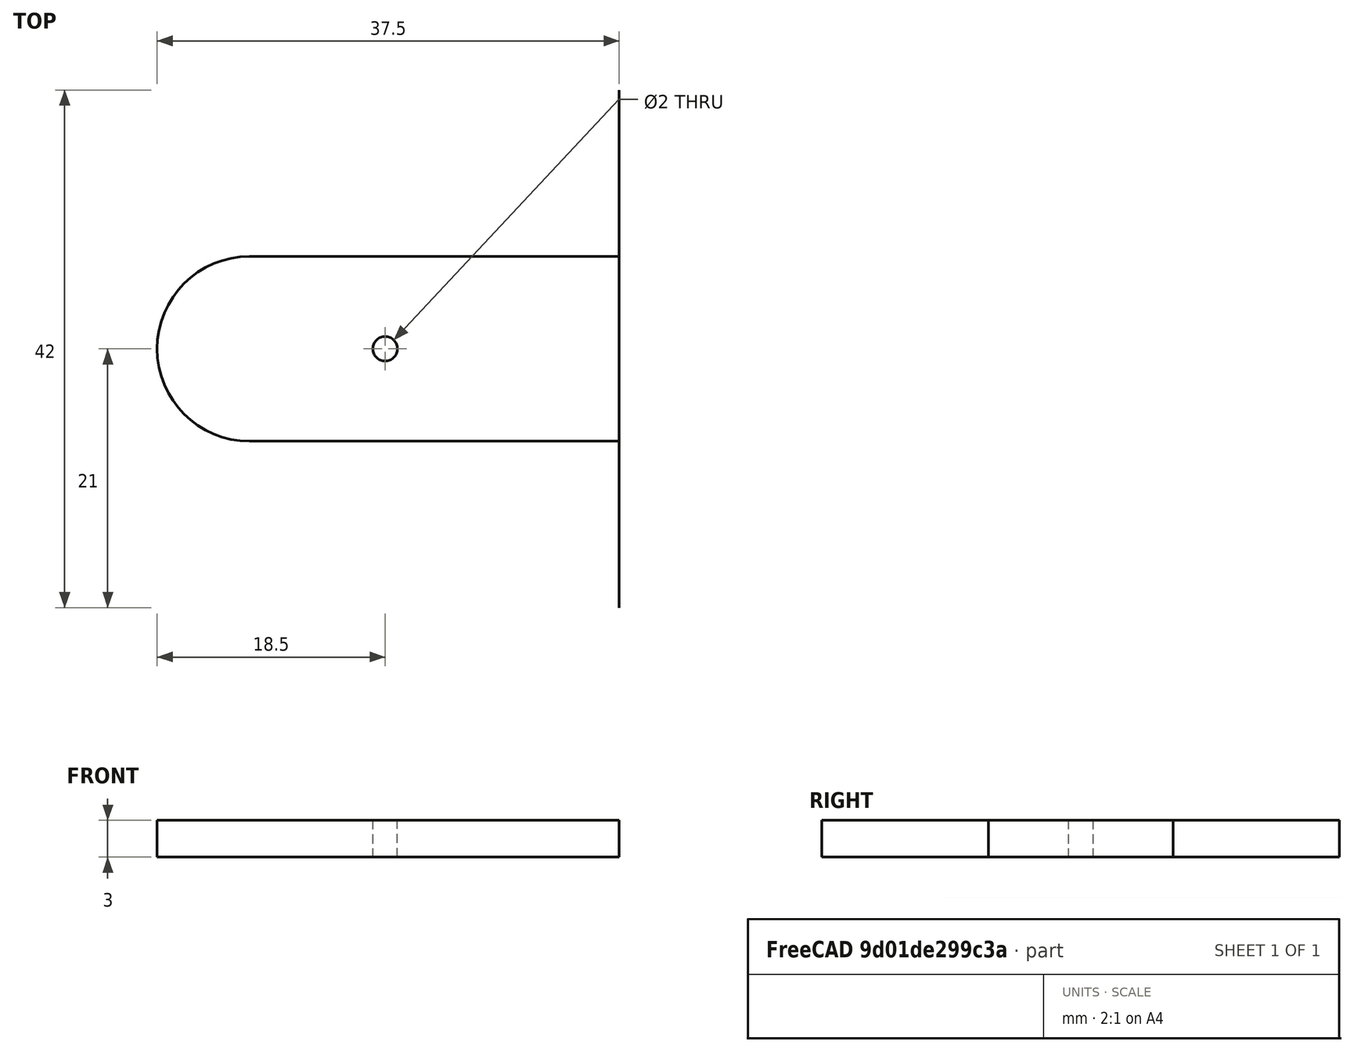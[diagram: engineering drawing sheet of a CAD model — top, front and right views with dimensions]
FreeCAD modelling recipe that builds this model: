
FCSTD DOCUMENT  (FreeCAD 0.18R4 (GitTag))
Label: Horizontal Servo Base
License: All rights reserved
LicenseURL: http://en.wikipedia.org/wiki/All_rights_reserved
objects: Sketcher::SketchObject×1, Part::Extrusion×1
note: 2 computed .brp shape members not serialized (recipe doc carries the construction recipe); baked Part::Feature solids carry a one-line shape summary decoded from their .brp

FEATURE [Sketcher::SketchObject] Sketch
  sketch-geometry (5):
    g0: LineSegment StartX=19 StartY=21 StartZ=0 EndX=19 EndY=-21 EndZ=0
    g1: ArcOfCircle CenterX=-11 CenterY=4e-16 CenterZ=0 NormalX=0 NormalY=0 NormalZ=1 AngleXU=0 Radius=7.5 StartAngle=1.5708 EndAngle=4.71239
    g2: LineSegment StartX=19 StartY=7.5 StartZ=0 EndX=-11 EndY=7.5 EndZ=0
    g3: LineSegment StartX=19 StartY=-7.5 StartZ=0 EndX=-11 EndY=-7.5 EndZ=0
    g4: Circle CenterX=0 CenterY=0 CenterZ=0 NormalX=0 NormalY=0 NormalZ=1 AngleXU=0 Radius=1
  constraints (13):
    c: DistanceY(g0,g0) = 42
    c: Symmetric(g0,g0,g-1)
    c: Tangent(g2,g1) = -1.5708
    c: Tangent(g3,g1) = 1.5708
    c: Horizontal(g2)
    c: DistanceX(g-1,g0) = 19
    c: DistanceY(g1,g1) = 15
    c: Symmetric(g1,g1,g-1)
    c: Equal(g3,g2)
    c: DistanceX(g1,g3) = 30
    c: PointOnObject(g2,g0)
    c: Radius(g4) = 1
    c: Coincident(g4,g-1)
FEATURE [Part::Extrusion] Extrude
  Base = -> Sketch
  Dir = (0,0,1)
  DirMode = 2
  FaceMakerClass = Part::FaceMakerBullseye
  LengthFwd = 3
  LengthRev = 0
  Solid = false
  Symmetric = false
